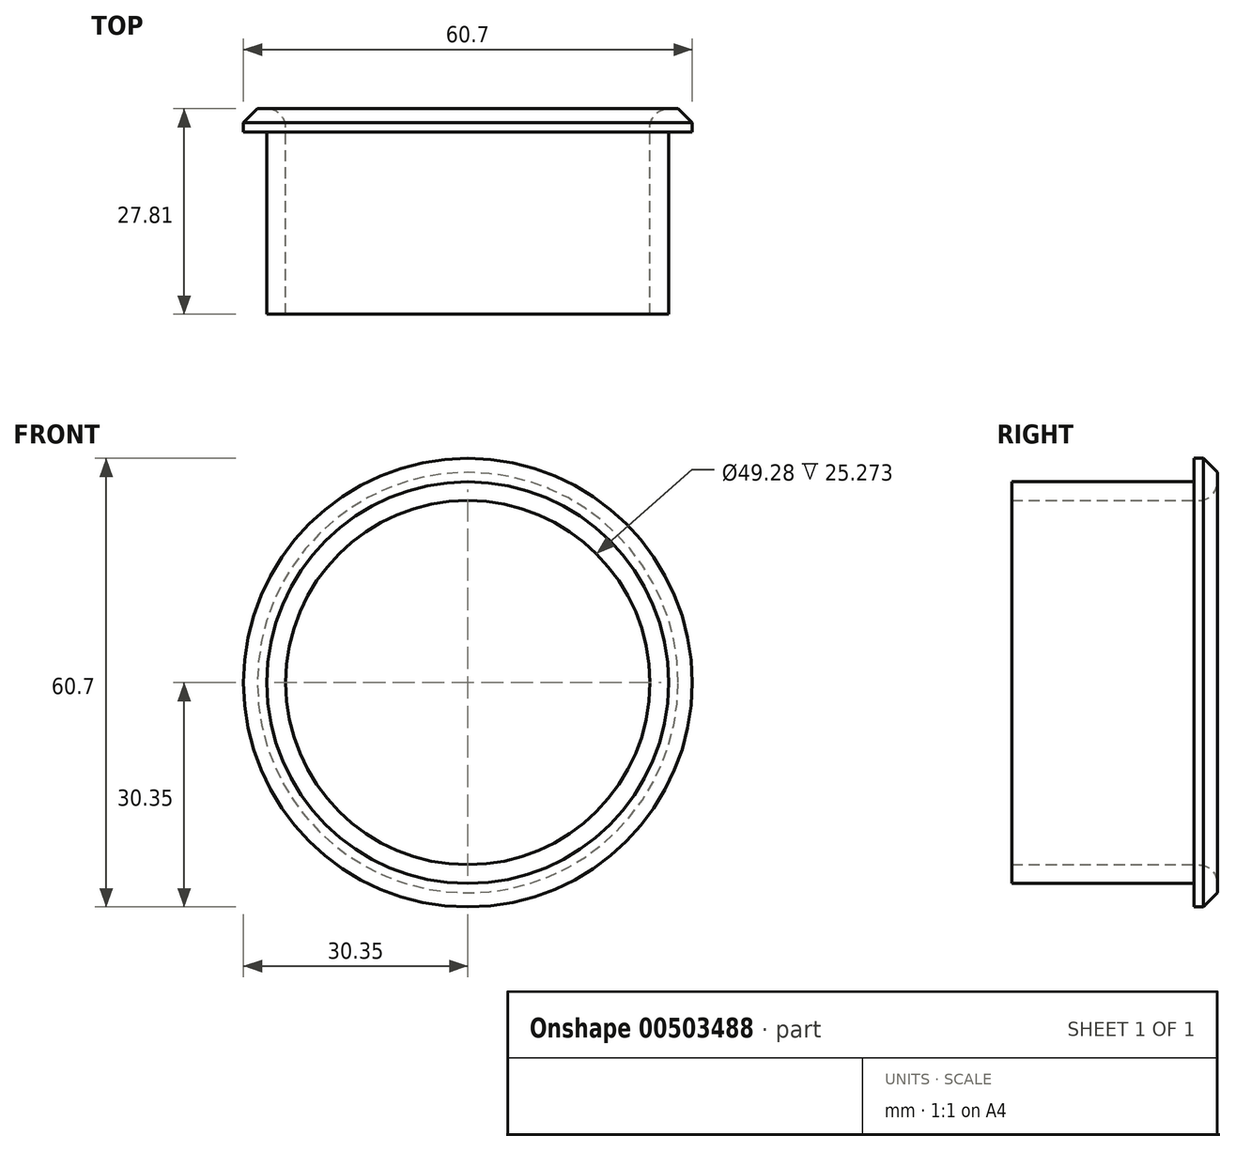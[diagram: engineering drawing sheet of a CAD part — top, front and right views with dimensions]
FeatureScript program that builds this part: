
annotation { "Feature Type Name" : "Feature", "Feature Type Description" : "" }
export const myFeature = defineFeature(function(context is Context, id is Id, definition is map)
    precondition{}
    {
        {
            var Q0;
            Q0=qCreatedBy(makeId("Front.planeOp"),FACE);
            var sketch = newSketch(context, id + "F0", { "sketchPlane" : qUnion([Q0])});
            skCircle(sketch, "E0", {"center": v(0, 0) * mm, "radius": 27.18 * mm});
            skCircle(sketch, "E1", {"center": v(0, 0) * mm, "radius": 30.35 * mm});
            skCircle(sketch, "E2", {"center": v(0, 0) * mm, "radius": 24.64 * mm});
            skSolve(sketch);
        }
        {
            var Q0;
            Q0=makeQuery(id+"F0.imprint","IMPRINT",FACE,{"disambiguationData":[TD([[makeQuery(id+"F0.imprint","IMPRINT",EDGE,{"derivedFrom":sQuery(id+"F0.wireOp",EDGE,"E0")}),1.0]])]});
            extrude(context, id + "F1", {"entities" : qUnion([Q0]), "depth" : 27.8 * mm});
        }
        {
            var Q0;
            Q0=makeQuery(id+"F0.imprint","IMPRINT",FACE,{"disambiguationData":[TD([[makeQuery(id+"F0.imprint","IMPRINT",EDGE,{"derivedFrom":sQuery(id+"F0.wireOp",EDGE,"E0")}),-1.0]])]});
            extrude(context, id + "F2", {"entities" : qUnion([Q0]), "operationType" : NewBodyOperationType.ADD, "depth" : 3.17 * mm});
        }
        {
            var Q0;
            Q0=makeQuery(id+"F1.opExtrude","CAP_EDGE",EDGE,{"disambiguationData":[OSD([sQuery(id+"F0.wireOp",EDGE,"E2")])],"isStart":true});
            fillet(context, id + "F3", {"entities" : qUnion([Q0]), "radius" : 2.54 * mm, "tangentPropagation" : true, "allowEdgeOverflow" : false});
        }
        {
            var Q0;
            Q0=makeQuery(id+"F2.opExtrude","CAP_EDGE",EDGE,{"disambiguationData":[OSD([sQuery(id+"F0.wireOp",EDGE,"E1")])],"isStart":true});
            chamfer(context, id + "F4", {"entities" : qUnion([Q0]), "width" : 1.9 * mm, "tangentPropagation" : true});
        }
    });
